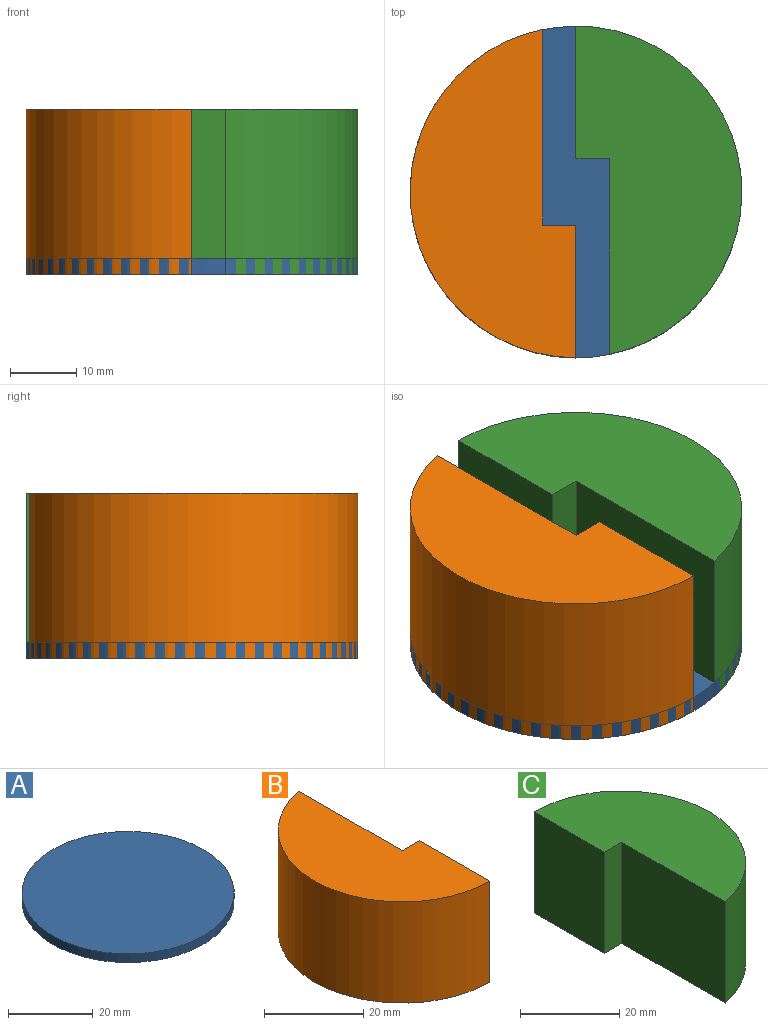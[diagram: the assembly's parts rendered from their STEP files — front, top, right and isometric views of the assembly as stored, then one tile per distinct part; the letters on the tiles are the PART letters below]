
ASSEMBLY  parts=3 mates=2
PART A: 3 faces, bbox 50x50x2.5 mm
  f0: cylinder r=25mm len=50mm, axis (0,0,-1), area 392.7mm2, adj f1,f2
  f1: plane 50x50mm, normal (0,0,1), area 1963.5mm2, adj f0
  f2: plane 50x50mm, normal (0,0,-1), area 1963.5mm2, adj f0
PART B: 6 faces, bbox 25x49.5x25 mm
  f0: plane 29.5x25mm, normal (1,0,0), area 737.4mm2, adj f1,f3,f4,f5
  f1: cylinder r=25mm len=49.5mm, axis (0,0,-1), area 1837.6mm2, adj f0,f2,f4,f5
  f2: plane 25x20mm, normal (1,0,0), area 500mm2, adj f1,f3,f4,f5
  f3: plane 25x5mm, normal (0,1,0), area 125mm2, adj f0,f2,f4,f5
  f4: plane 49.5x25mm, normal (0,0,1), area 832.6mm2, adj f0,f1,f2,f3
  f5: plane 49.5x25mm, normal (0,0,-1), area 832.6mm2, adj f0,f1,f2,f3
PART C: 6 faces, bbox 25x49.5x25 mm
  f0: plane 29.5x25mm, normal (-1,0,0), area 737.4mm2, adj f1,f3,f4,f5
  f1: cylinder r=25mm len=49.5mm, axis (0,0,-1), area 1837.6mm2, adj f0,f2,f4,f5
  f2: plane 25x20mm, normal (-1,0,0), area 500mm2, adj f1,f3,f4,f5
  f3: plane 25x5mm, normal (0,-1,0), area 125mm2, adj f0,f2,f4,f5
  f4: plane 49.5x25mm, normal (0,0,1), area 832.6mm2, adj f0,f1,f2,f3
  f5: plane 49.5x25mm, normal (0,0,-1), area 832.6mm2, adj f0,f1,f2,f3
PLACE A t=(-47.82,-7.34,30.94)mm
PLACE B t=(-47.82,-7.34,30.94)mm
PLACE C t=(-47.82,-7.34,30.94)mm
MATE fastened C.f1 <-> A.f0  axis (0,0,-1) through (-47.82,-7.34,30.94)mm
MATE fastened B.f1 <-> A.f0  axis (0,0,-1) through (-47.82,-7.34,30.94)mm
